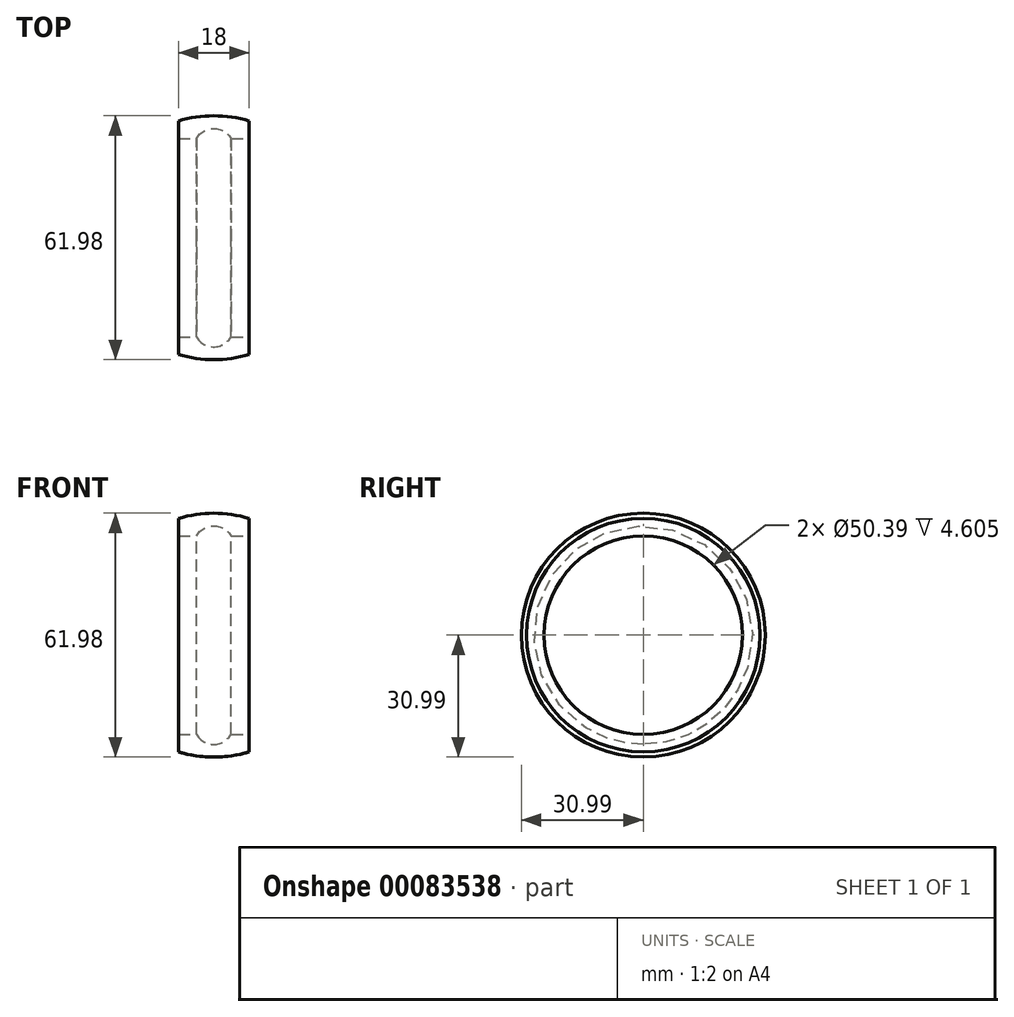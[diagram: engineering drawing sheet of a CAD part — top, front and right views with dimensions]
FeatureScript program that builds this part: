
annotation { "Feature Type Name" : "Feature", "Feature Type Description" : "" }
export const myFeature = defineFeature(function(context is Context, id is Id, definition is map)
    precondition{}
    {
        {
            var Q0;
            Q0=qCreatedBy(makeId("Front.planeOp"),FACE);
            var sketch = newSketch(context, id + "F0", { "sketchPlane" : qUnion([Q0])});
            skArc(sketch, "E0", {"start": v(9, 29.65) * mm, "mid": v(0, 30.99) * mm, "end": v(-9, 29.65) * mm});
            skLineSegment(sketch, "E1", {"start": v(0, 0) * mm, "end": v(9, 0) * mm});
            skLineSegment(sketch, "E2", {"start": v(9, 29.65) * mm, "end": v(9, 25.2) * mm});
            skLineSegment(sketch, "E3.MirrorCS", {"start": v(0, 0) * mm, "end": v(-9, 0) * mm});
            skLineSegment(sketch, "E4.MirrorCS", {"start": v(-9, 29.65) * mm, "end": v(-9, 25.2) * mm});
            skLineSegment(sketch, "E5", {"start": v(-9, 25.2) * mm, "end": v(-4.4, 25.2) * mm});
            skArc(sketch, "E6", {"start": v(4.4, 25.2) * mm, "mid": v(0, 27.74) * mm, "end": v(-4.4, 25.2) * mm});
            skLineSegment(sketch, "E7.trimOffspring", {"start": v(4.4, 25.2) * mm, "end": v(9, 25.2) * mm});
            skPoint(sketch, "E8.start.orphan", {"position": v(0, 25.2) * mm});
            skPoint(sketch, "E9.orphan", {"position": v(-9, 0) * mm});
            skSolve(sketch);
        }
        {
            var Q0;
            Q0=makeQuery(id+"F0.imprint","IMPRINT",FACE,{"disambiguationData":[TD([[makeQuery(id+"F0.imprint","IMPRINT",EDGE,{"derivedFrom":sQuery(id+"F0.wireOp",EDGE,"E0")}),1.0]])]});
            var Q1;
            Q1=sQuery(id+"F0.wireOp",EDGE,"E3.MirrorCS");
            revolve(context, id + "F1", {"entities" : qUnion([Q0]), "axis" : qUnion([Q1]), "revolveType" : RevolveType.FULL});
        }
    });
